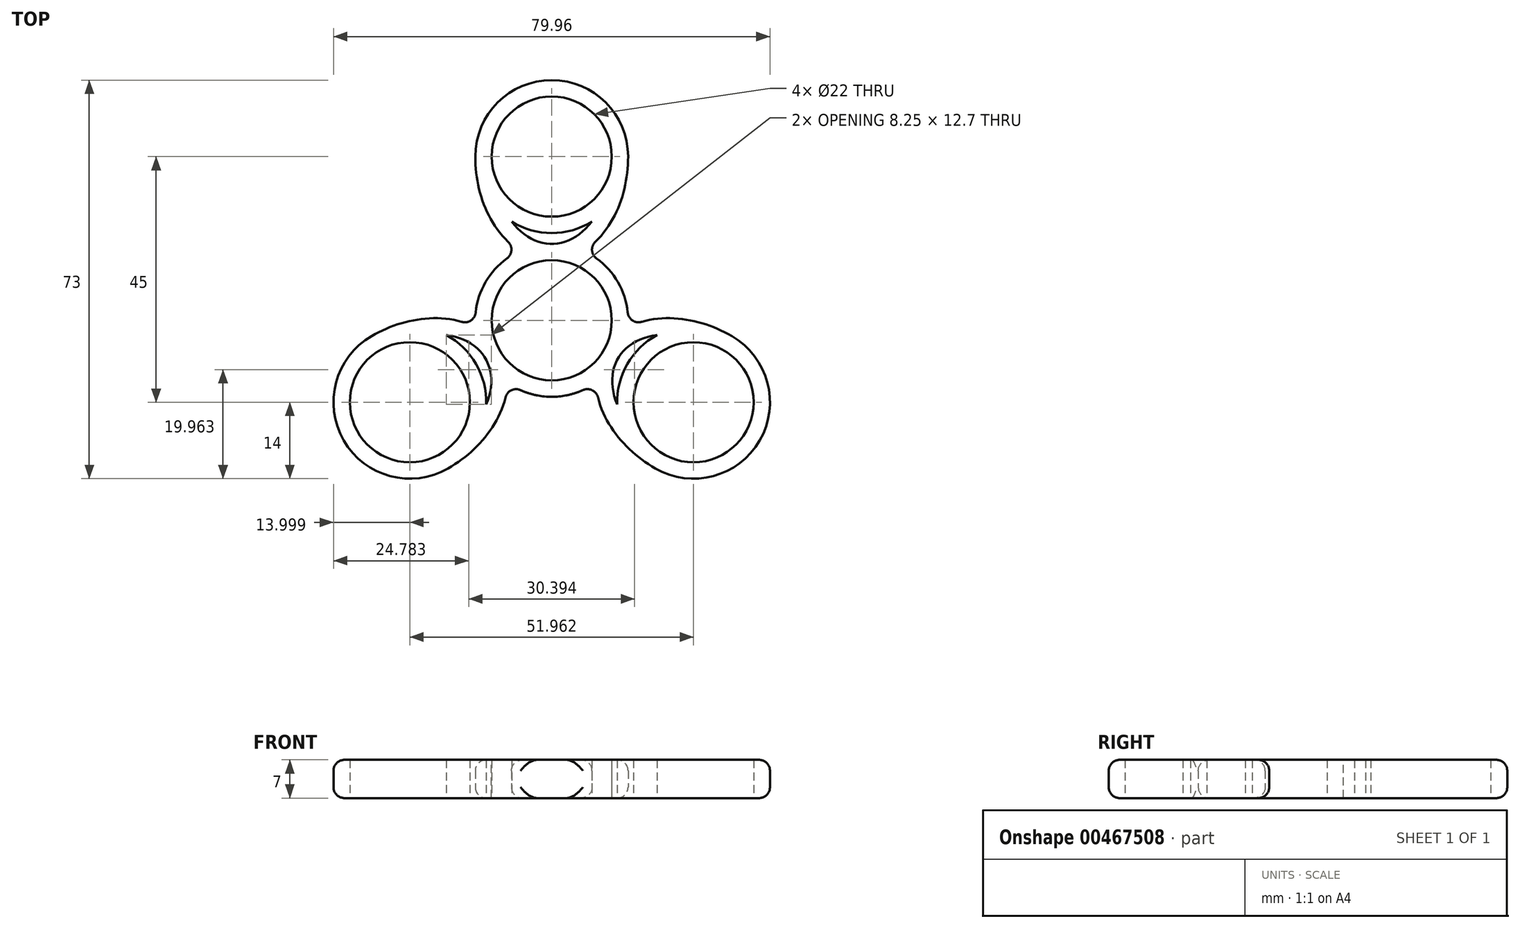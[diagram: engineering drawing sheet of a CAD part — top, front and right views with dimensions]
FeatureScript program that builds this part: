
annotation { "Feature Type Name" : "Feature", "Feature Type Description" : "" }
export const myFeature = defineFeature(function(context is Context, id is Id, definition is map)
    precondition{}
    {
        {
            var Q0;
            Q0=qCreatedBy(makeId("Top.planeOp"),FACE);
            var sketch = newSketch(context, id + "F0", { "sketchPlane" : qUnion([Q0])});
            skCircle(sketch, "E0", {"center": v(0, 0) * mm, "radius": 11 * mm});
            skCircle(sketch, "E1", {"center": v(0, 30) * mm, "radius": 11 * mm});
            skArc(sketch, "E2.0", {"start": v(-7.33, 18.07) * mm, "mid": v(0, 16) * mm, "end": v(7.33, 18.07) * mm});
            skArc(sketch, "E3.0", {"start": v(-5.83, 12.73) * mm, "mid": v(-12.23, 6.81) * mm, "end": v(-13.9, -1.74) * mm});
            skPoint(sketch, "E4", {"position": v(0, 11) * mm});
            skPoint(sketch, "E5", {"position": v(0, 14) * mm});
            skPoint(sketch, "E6", {"position": v(11, 30) * mm});
            skPoint(sketch, "E7", {"position": v(14, 30) * mm});
            skPoint(sketch, "E8", {"position": v(-11, 30) * mm});
            skPoint(sketch, "E9", {"position": v(-14, 30) * mm});
            skEllipticalArc(sketch, "E10", {});
            skEllipticalArc(sketch, "E11", {});
            skArc(sketch, "E12.trimOffspring", {"start": v(14, 30) * mm, "mid": v(0, 44) * mm, "end": v(-14, 30) * mm});
            skEllipticalArc(sketch, "E13.trimOffspring", {});
            skArc(sketch, "E14.trimOffspring", {"start": v(-8.45, -11.16) * mm, "mid": v(0, -14) * mm, "end": v(8.45, -11.16) * mm});
            skArc(sketch, "E15.trimOffspring", {"start": v(13.9, -1.74) * mm, "mid": v(12.23, 6.81) * mm, "end": v(5.83, 12.73) * mm});
            skArc(sketch, "E16", {"start": v(-13.9, -1.74) * mm, "mid": v(-12.12, -7) * mm, "end": v(-8.45, -11.16) * mm});
            skArc(sketch, "E17", {"start": v(8.45, -11.16) * mm, "mid": v(12.12, -7) * mm, "end": v(13.9, -1.74) * mm});
            skCircle(sketch, "E18.1.0", {"center": v(-25.98, -15) * mm, "radius": 11 * mm});
            skArc(sketch, "E18.1.1", {"start": v(-11.99, -15.39) * mm, "mid": v(-13.86, -8) * mm, "end": v(-19.32, -2.69) * mm});
            skEllipticalArc(sketch, "E18.1.2", {});
            skEllipticalArc(sketch, "E18.1.3", {});
            skArc(sketch, "E18.1.4", {"start": v(-32.98, -2.88) * mm, "mid": v(-38.1, -22) * mm, "end": v(-18.98, -27.12) * mm});
            skEllipticalArc(sketch, "E18.1.5", {});
            skCircle(sketch, "E18.2.0", {"center": v(25.98, -15) * mm, "radius": 11 * mm});
            skArc(sketch, "E18.2.1", {"start": v(19.32, -2.69) * mm, "mid": v(13.86, -8) * mm, "end": v(11.99, -15.39) * mm});
            skEllipticalArc(sketch, "E18.2.2", {});
            skEllipticalArc(sketch, "E18.2.3", {});
            skArc(sketch, "E18.2.4", {"start": v(18.98, -27.12) * mm, "mid": v(38.1, -22) * mm, "end": v(32.98, -2.88) * mm});
            skEllipticalArc(sketch, "E18.2.5", {});
            const initialGuessF0  = {"E10": [0, 0.03, 1, 0, 0.014, 0.019, 3.141592653589793, 4.282689314233266], "E11": [0, 0.03, 1, 0, 0.011, 0.016, 3.9826613241577244, 5.4421166366116545], "E13.trimOffspring": [0, 0.03, 1, 0, 0.014, 0.019, 5.142088646536115, 6.283185307179586], "E18.1.2": [-0.02598076211353316, -0.015, -0.5, 0.8660254037844389, 0.011, 0.016, 3.9826613241577244, 5.4421166366116545], "E18.1.3": [-0.02598076211353316, -0.015, -0.5, 0.8660254037844389, 0.014, 0.019, 5.142088646536115, 6.283185307179586], "E18.1.5": [-0.02598076211353316, -0.015, -0.5, 0.8660254037844389, 0.014, 0.019, 3.141592653589793, 4.282689314233266], "E18.2.2": [0.02598076211353315, -0.015, -0.5, -0.8660254037844384, 0.011, 0.016, 3.9826613241577244, 5.4421166366116545], "E18.2.3": [0.02598076211353315, -0.015, -0.5, -0.8660254037844384, 0.014, 0.019, 5.142088646536115, 6.283185307179586], "E18.2.5": [0.02598076211353315, -0.015, -0.5, -0.8660254037844384, 0.014, 0.019, 3.141592653589793, 4.282689314233266]};
            skSetInitialGuess(sketch, initialGuessF0);
            skSolve(sketch);
        }
        {
            var Q0;
            Q0=makeQuery(id+"F0.imprint","IMPRINT",FACE,{"disambiguationData":[TD([[makeQuery(id+"F0.imprint","IMPRINT",EDGE,{"derivedFrom":sQuery(id+"F0.wireOp",EDGE,"E0")}),-1.0]])]});
            var Q1;
            Q1=makeQuery(id+"F0.imprint","IMPRINT",FACE,{"disambiguationData":[TD([[makeQuery(id+"F0.imprint","IMPRINT",EDGE,{"derivedFrom":sQuery(id+"F0.wireOp",EDGE,"E18.1.0")}),-1.0]])]});
            var Q2;
            Q2=makeQuery(id+"F0.imprint","IMPRINT",FACE,{"disambiguationData":[TD([[makeQuery(id+"F0.imprint","IMPRINT",EDGE,{"derivedFrom":sQuery(id+"F0.wireOp",EDGE,"E18.2.0")}),-1.0]])]});
            extrude(context, id + "F1", {"entities" : qUnion([Q0, Q1, Q2]), "endBound" : BoundingType.SYMMETRIC, "depth" : 7 * mm});
        }
        {
            var Q0;
            Q0=makeQuery(id+"F1.opExtrude","SWEPT_FACE",FACE,{"disambiguationData":[OSD([sQuery(id+"F0.wireOp",EDGE,"E10")])]});
            var Q1;
            Q1=makeQuery(id+"F1.opExtrude","SWEPT_FACE",FACE,{"disambiguationData":[OSD([sQuery(id+"F0.wireOp",EDGE,"E12.trimOffspring")])]});
            var Q2;
            Q2=makeQuery(id+"F1.opExtrude","SWEPT_FACE",FACE,{"disambiguationData":[OSD([sQuery(id+"F0.wireOp",EDGE,"E18.1.4")])]});
            var Q3;
            Q3=makeQuery(id+"F1.opExtrude","SWEPT_FACE",FACE,{"disambiguationData":[OSD([sQuery(id+"F0.wireOp",EDGE,"E18.1.5")])]});
            var Q4;
            Q4=makeQuery(id+"F1.opExtrude","SWEPT_FACE",FACE,{"disambiguationData":[OSD([sQuery(id+"F0.wireOp",EDGE,"E3.0")])]});
            var Q5;
            Q5=makeQuery(id+"F1.opExtrude","SWEPT_FACE",FACE,{"disambiguationData":[OSD([sQuery(id+"F0.wireOp",EDGE,"E18.1.3")])]});
            var Q6;
            Q6=makeQuery(id+"F1.opExtrude","SWEPT_FACE",FACE,{"disambiguationData":[OSD([sQuery(id+"F0.wireOp",EDGE,"E18.2.3")])]});
            var Q7;
            Q7=makeQuery(id+"F1.opExtrude","SWEPT_FACE",FACE,{"disambiguationData":[OSD([sQuery(id+"F0.wireOp",EDGE,"E18.2.4")])]});
            var Q8;
            Q8=makeQuery(id+"F1.opExtrude","SWEPT_FACE",FACE,{"disambiguationData":[OSD([sQuery(id+"F0.wireOp",EDGE,"E15.trimOffspring")])]});
            fillet(context, id + "F2", {"entities" : qUnion([Q0, Q1, Q2, Q3, Q4, Q5, Q6, Q7, Q8]), "radius" : 2 * mm, "tangentPropagation" : true, "allowEdgeOverflow" : false});
        }
    });
